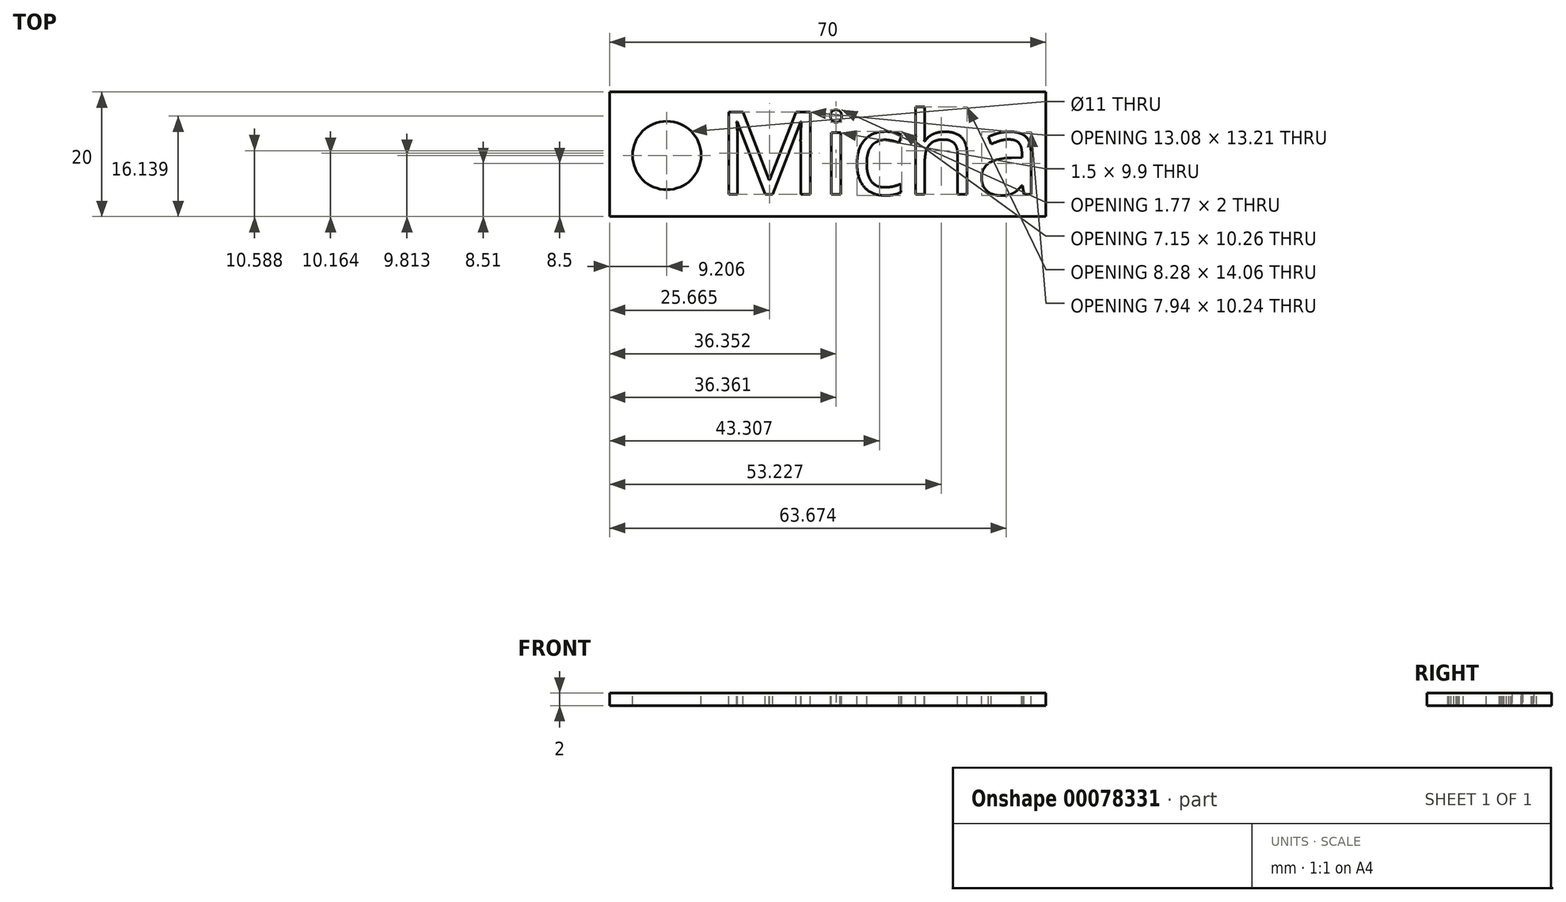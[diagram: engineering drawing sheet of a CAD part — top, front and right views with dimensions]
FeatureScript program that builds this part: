
annotation { "Feature Type Name" : "Feature", "Feature Type Description" : "" }
export const myFeature = defineFeature(function(context is Context, id is Id, definition is map)
    precondition{}
    {
        {
            var Q0;
            Q0=qCreatedBy(makeId("Top.planeOp"),FACE);
            var sketch = newSketch(context, id + "F0", { "sketchPlane" : qUnion([Q0])});
            skLineSegment(sketch, "E0.bottom", {"start": v(-70, 20) * mm, "end": v(0, 20) * mm});
            skLineSegment(sketch, "E0.top", {"start": v(-70, 0) * mm, "end": v(0, 0) * mm});
            skLineSegment(sketch, "E0.left", {"start": v(-70, 20) * mm, "end": v(-70, 0) * mm});
            skLineSegment(sketch, "E0.right", {"start": v(0, 20) * mm, "end": v(0, 0) * mm});
            skText(sketch, "E1", { "text": "Micha\n", "fontName": "OpenSans-Regular.ttf"});
            const initialGuessF0  = {"E1": [-0.05269, 0.00356, 1, 0, 0.01332]};
            skSetInitialGuess(sketch, initialGuessF0);
            skSolve(sketch);
        }
        {
            var Q0;
            Q0=makeQuery(id+"F0.imprint","IMPRINT",FACE,{"disambiguationData":[TD([[makeQuery(id+"F0.imprint","IMPRINT",EDGE,{"derivedFrom":sQuery(id+"F0.wireOp",EDGE,"E0.bottom")}),-1.0]])]});
            var sketch = newSketch(context, id + "F1", { "sketchPlane" : qUnion([Q0])});
            skPoint(sketch, "E2", {"position": v(-60.8, 9.81) * mm});
            skSolve(sketch);
        }
        {
            var Q0;
            Q0 = qSketchRegion(id + "F0", true);
            extrude(context, id + "F2", {"entities" : qUnion([Q0]), "oppositeDirection" : true, "depth" : 2 * mm});
        }
        {
            var Q0;
            Q0=sQuery(id+"F1.wireOp",VERTEX,"E2");
            var Q1;
            Q1=makeQuery(id+"F2.opExtrude","SWEPT_BODY",BODY,{"disambiguationData":[OSD([sQuery(id+"F0.wireOp",EDGE,"E0.bottom"),sQuery(id+"F0.wireOp",EDGE,"E0.top"),sQuery(id+"F0.wireOp",EDGE,"E0.left"),sQuery(id+"F0.wireOp",EDGE,"E0.right"),sQuery(id+"F0.wireOp",EDGE,"E1.sketch_text.stroke-0"),sQuery(id+"F0.wireOp",EDGE,"E1.sketch_text.stroke-1"),sQuery(id+"F0.wireOp",EDGE,"E1.sketch_text.stroke-2"),sQuery(id+"F0.wireOp",EDGE,"E1.sketch_text.stroke-3"),sQuery(id+"F0.wireOp",EDGE,"E1.sketch_text.stroke-4"),sQuery(id+"F0.wireOp",EDGE,"E1.sketch_text.stroke-5"),sQuery(id+"F0.wireOp",EDGE,"E1.sketch_text.stroke-6"),sQuery(id+"F0.wireOp",EDGE,"E1.sketch_text.stroke-7"),sQuery(id+"F0.wireOp",EDGE,"E1.sketch_text.stroke-8"),sQuery(id+"F0.wireOp",EDGE,"E1.sketch_text.stroke-9"),sQuery(id+"F0.wireOp",EDGE,"E1.sketch_text.stroke-10"),sQuery(id+"F0.wireOp",EDGE,"E1.sketch_text.stroke-11"),sQuery(id+"F0.wireOp",EDGE,"E1.sketch_text.stroke-12"),sQuery(id+"F0.wireOp",EDGE,"E1.sketch_text.stroke-13"),sQuery(id+"F0.wireOp",EDGE,"E1.sketch_text.stroke-14"),sQuery(id+"F0.wireOp",EDGE,"E1.sketch_text.stroke-15"),sQuery(id+"F0.wireOp",EDGE,"E1.sketch_text.stroke-16"),sQuery(id+"F0.wireOp",EDGE,"E1.sketch_text.stroke-17"),sQuery(id+"F0.wireOp",EDGE,"E1.sketch_text.stroke-18"),sQuery(id+"F0.wireOp",EDGE,"E1.sketch_text.stroke-19"),sQuery(id+"F0.wireOp",EDGE,"E1.sketch_text.stroke-20"),sQuery(id+"F0.wireOp",EDGE,"E1.sketch_text.stroke-21"),sQuery(id+"F0.wireOp",EDGE,"E1.sketch_text.stroke-22"),sQuery(id+"F0.wireOp",EDGE,"E1.sketch_text.stroke-23"),sQuery(id+"F0.wireOp",EDGE,"E1.sketch_text.stroke-24"),sQuery(id+"F0.wireOp",EDGE,"E1.sketch_text.stroke-25"),sQuery(id+"F0.wireOp",EDGE,"E1.sketch_text.stroke-26"),sQuery(id+"F0.wireOp",EDGE,"E1.sketch_text.stroke-27"),sQuery(id+"F0.wireOp",EDGE,"E1.sketch_text.stroke-28"),sQuery(id+"F0.wireOp",EDGE,"E1.sketch_text.stroke-29"),sQuery(id+"F0.wireOp",EDGE,"E1.sketch_text.stroke-30"),sQuery(id+"F0.wireOp",EDGE,"E1.sketch_text.stroke-31"),sQuery(id+"F0.wireOp",EDGE,"E1.sketch_text.stroke-32"),sQuery(id+"F0.wireOp",EDGE,"E1.sketch_text.stroke-33"),sQuery(id+"F0.wireOp",EDGE,"E1.sketch_text.stroke-34"),sQuery(id+"F0.wireOp",EDGE,"E1.sketch_text.stroke-35"),sQuery(id+"F0.wireOp",EDGE,"E1.sketch_text.stroke-36"),sQuery(id+"F0.wireOp",EDGE,"E1.sketch_text.stroke-37"),sQuery(id+"F0.wireOp",EDGE,"E1.sketch_text.stroke-38"),sQuery(id+"F0.wireOp",EDGE,"E1.sketch_text.stroke-39"),sQuery(id+"F0.wireOp",EDGE,"E1.sketch_text.stroke-40"),sQuery(id+"F0.wireOp",EDGE,"E1.sketch_text.stroke-41"),sQuery(id+"F0.wireOp",EDGE,"E1.sketch_text.stroke-42"),sQuery(id+"F0.wireOp",EDGE,"E1.sketch_text.stroke-43"),sQuery(id+"F0.wireOp",EDGE,"E1.sketch_text.stroke-44"),sQuery(id+"F0.wireOp",EDGE,"E1.sketch_text.stroke-45"),sQuery(id+"F0.wireOp",EDGE,"E1.sketch_text.stroke-46"),sQuery(id+"F0.wireOp",EDGE,"E1.sketch_text.stroke-47"),sQuery(id+"F0.wireOp",EDGE,"E1.sketch_text.stroke-48"),sQuery(id+"F0.wireOp",EDGE,"E1.sketch_text.stroke-49"),sQuery(id+"F0.wireOp",EDGE,"E1.sketch_text.stroke-50"),sQuery(id+"F0.wireOp",EDGE,"E1.sketch_text.stroke-51"),sQuery(id+"F0.wireOp",EDGE,"E1.sketch_text.stroke-52"),sQuery(id+"F0.wireOp",EDGE,"E1.sketch_text.stroke-53"),sQuery(id+"F0.wireOp",EDGE,"E1.sketch_text.stroke-54"),sQuery(id+"F0.wireOp",EDGE,"E1.sketch_text.stroke-55"),sQuery(id+"F0.wireOp",EDGE,"E1.sketch_text.stroke-56"),sQuery(id+"F0.wireOp",EDGE,"E1.sketch_text.stroke-57"),sQuery(id+"F0.wireOp",EDGE,"E1.sketch_text.stroke-58"),sQuery(id+"F0.wireOp",EDGE,"E1.sketch_text.stroke-59"),sQuery(id+"F0.wireOp",EDGE,"E1.sketch_text.stroke-60"),sQuery(id+"F0.wireOp",EDGE,"E1.sketch_text.stroke-61"),sQuery(id+"F0.wireOp",EDGE,"E1.sketch_text.stroke-62"),sQuery(id+"F0.wireOp",EDGE,"E1.sketch_text.stroke-63"),sQuery(id+"F0.wireOp",EDGE,"E1.sketch_text.stroke-64"),sQuery(id+"F0.wireOp",EDGE,"E1.sketch_text.stroke-65"),sQuery(id+"F0.wireOp",EDGE,"E1.sketch_text.stroke-66"),sQuery(id+"F0.wireOp",EDGE,"E1.sketch_text.stroke-67"),sQuery(id+"F0.wireOp",EDGE,"E1.sketch_text.stroke-68"),sQuery(id+"F0.wireOp",EDGE,"E1.sketch_text.stroke-69"),sQuery(id+"F0.wireOp",EDGE,"E1.sketch_text.stroke-70"),sQuery(id+"F0.wireOp",EDGE,"E1.sketch_text.stroke-71"),sQuery(id+"F0.wireOp",EDGE,"E1.sketch_text.stroke-72"),sQuery(id+"F0.wireOp",EDGE,"E1.sketch_text.stroke-73"),sQuery(id+"F0.wireOp",EDGE,"E1.sketch_text.stroke-74"),sQuery(id+"F0.wireOp",EDGE,"E1.sketch_text.stroke-75"),sQuery(id+"F0.wireOp",EDGE,"E1.sketch_text.stroke-76"),sQuery(id+"F0.wireOp",EDGE,"E1.sketch_text.stroke-77"),sQuery(id+"F0.wireOp",EDGE,"E1.sketch_text.stroke-78"),sQuery(id+"F0.wireOp",EDGE,"E1.sketch_text.stroke-79"),sQuery(id+"F0.wireOp",EDGE,"E1.sketch_text.stroke-80"),sQuery(id+"F0.wireOp",EDGE,"E1.sketch_text.stroke-81")])]});
            hole(context, id + "F3", {"style" : HoleStyle.SIMPLE, "endStyle" : HoleEndStyle.BLIND, "holeDiameter" : 11 * mm, "holeDepth" : 17 * mm, "locations" : qUnion([Q0]), "scope" : qUnion([Q1])});
        }
    });
